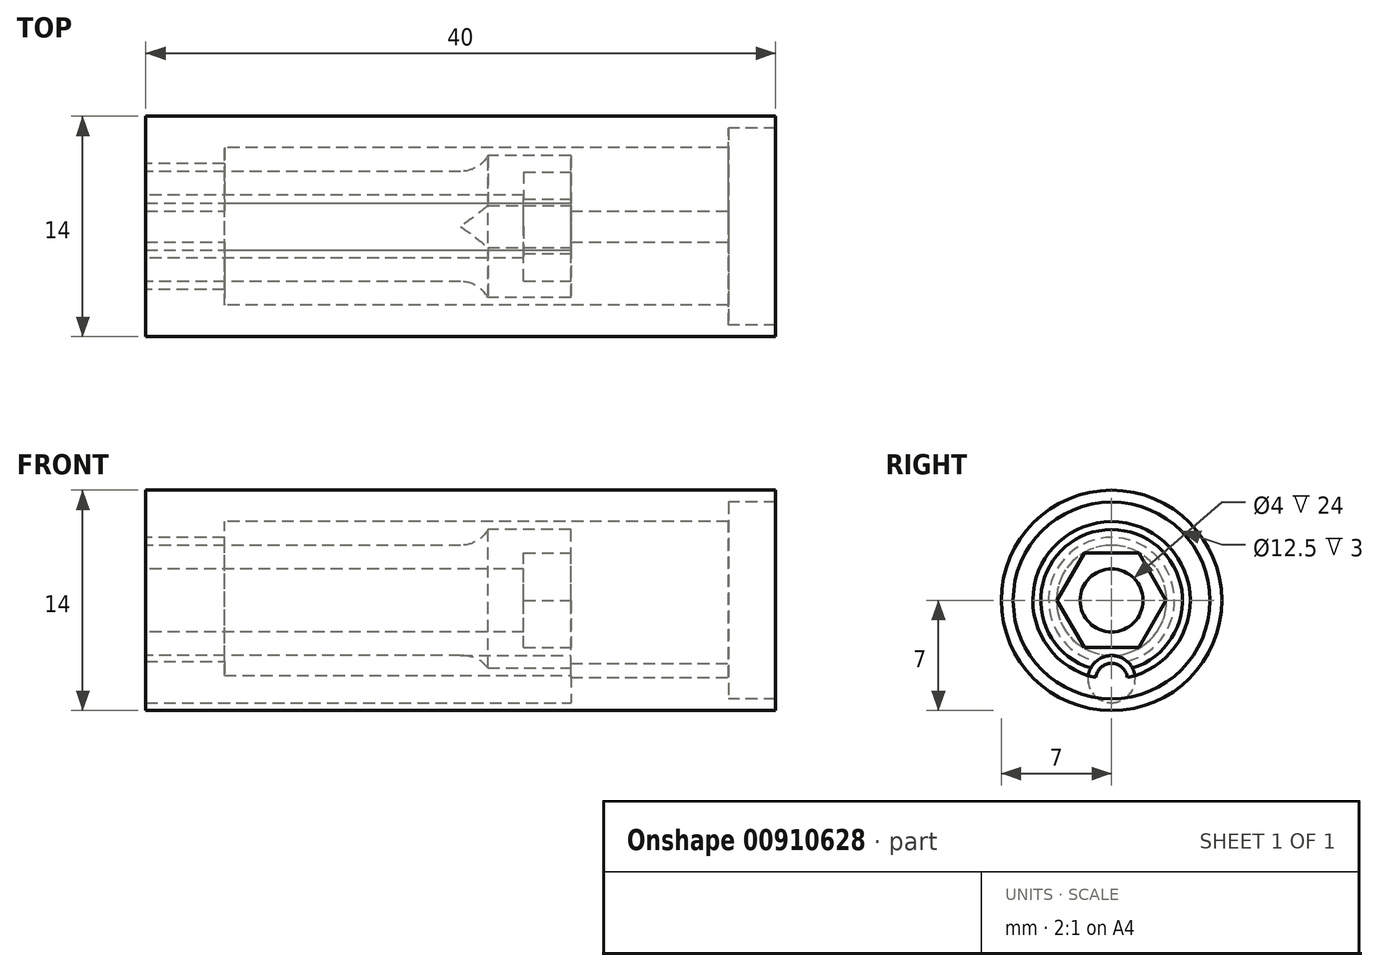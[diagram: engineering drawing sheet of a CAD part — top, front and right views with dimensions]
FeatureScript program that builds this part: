
annotation { "Feature Type Name" : "Feature", "Feature Type Description" : "" }
export const myFeature = defineFeature(function(context is Context, id is Id, definition is map)
    precondition{}
    {
        {
            var Q0;
            Q0=qCreatedBy(makeId("Front.planeOp"),FACE);
            var sketch = newSketch(context, id + "F0", { "sketchPlane" : qUnion([Q0])});
            skLineSegment(sketch, "E0", {"start": v(0, 0) * mm, "end": v(35.36, 0) * mm, "construction": true});
            skLineSegment(sketch, "E1.MirrorCS", {"start": v(40, -7) * mm, "end": v(0, -7) * mm});
            skLineSegment(sketch, "E2.MirrorCS", {"start": v(0, -3.5) * mm, "end": v(0, -2) * mm});
            skLineSegment(sketch, "E3.MirrorCS", {"start": v(0, -2) * mm, "end": v(27, -2) * mm});
            skLineSegment(sketch, "E4", {"start": v(0, -7) * mm, "end": v(0, -4) * mm});
            skLineSegment(sketch, "E5", {"start": v(0, -4) * mm, "end": v(5, -4) * mm});
            skLineSegment(sketch, "E6", {"start": v(5, -4) * mm, "end": v(5, -5) * mm});
            skLineSegment(sketch, "E7", {"start": v(0, -3.5) * mm, "end": v(22, -3.5) * mm});
            skLineSegment(sketch, "E8", {"start": v(22, -3.5) * mm, "end": v(22, -4.5) * mm});
            skLineSegment(sketch, "E9", {"start": v(22, -4.5) * mm, "end": v(27, -4.5) * mm});
            skLineSegment(sketch, "E10", {"start": v(27, -4.5) * mm, "end": v(27, -2) * mm});
            skLineSegment(sketch, "E11", {"start": v(40, -7) * mm, "end": v(40, -6.25) * mm});
            skLineSegment(sketch, "E12", {"start": v(40, -6.25) * mm, "end": v(37, -6.25) * mm});
            skLineSegment(sketch, "E13", {"start": v(37, -6.25) * mm, "end": v(37, -5) * mm});
            skLineSegment(sketch, "E14", {"start": v(37, -5) * mm, "end": v(5, -5) * mm});
            skSolve(sketch);
        }
        {
            var Q0;
            Q0=makeQuery(id+"F0.imprint","IMPRINT",FACE,{"disambiguationData":[TD([[makeQuery(id+"F0.imprint","IMPRINT",EDGE,{"derivedFrom":sQuery(id+"F0.wireOp",EDGE,"E1.MirrorCS")}),-1.0]])]});
            var Q1;
            Q1=makeQuery(id+"F0.imprint","IMPRINT",FACE,{"disambiguationData":[TD([[makeQuery(id+"F0.imprint","IMPRINT",EDGE,{"derivedFrom":sQuery(id+"F0.wireOp",EDGE,"E2.MirrorCS")}),-1.0]])]});
            var Q2;
            Q2=sQuery(id+"F0.wireOp",EDGE,"E0");
            revolve(context, id + "F1", {"surfaceOperationType" : NewSurfaceOperationType.NEW, "entities" : qUnion([Q0, Q1]), "axis" : qUnion([Q2]), "revolveType" : RevolveType.FULL});
        }
        {
            var Q0;
            Q0=makeQuery(id+"F1.opRevolve","SWEPT_FACE",FACE,{"disambiguationData":[OSD([sQuery(id+"F0.wireOp",EDGE,"E13")])]});
            var sketch = newSketch(context, id + "F2", { "sketchPlane" : qUnion([Q0])});
            skCircle(sketch, "E15", {"center": v(0, -5) * mm, "radius": 1 * mm});
            skSolve(sketch);
        }
        {
            var Q0;
            Q0 = qSketchRegion(id + "F2", true);
            var Q1;
            Q1=makeQuery(id+"F1.opRevolve","SWEPT_FACE",FACE,{"disambiguationData":[OSD([sQuery(id+"F0.wireOp",EDGE,"E4")])]});
            extrude(context, id + "F3", {"entities" : qUnion([Q0]), "operationType" : NewBodyOperationType.ADD, "endBound" : BoundingType.UP_TO_SURFACE, "oppositeDirection" : true, "depth" : 25 * mm, "endBoundEntityFace" : qUnion([Q1]), "offsetDistance" : 25 * mm});
        }
        {
            var Q0;
            Q0=makeQuery(id+"F1.opRevolve","SWEPT_EDGE",EDGE,{"disambiguationData":[OSD([sQuery(id+"F0.wireOp",EDGE,"E7"),sQuery(id+"F0.wireOp",EDGE,"E8")])]});
            fillet(context, id + "F4", {"entities" : qUnion([Q0]), "radius" : 2 * mm, "tangentPropagation" : true, "allowEdgeOverflow" : false});
        }
        {
            var Q0;
            Q0=makeQuery(id+"F1.opRevolve","SWEPT_FACE",FACE,{"disambiguationData":[OSD([sQuery(id+"F0.wireOp",EDGE,"E10")])]});
            var sketch = newSketch(context, id + "F5", { "sketchPlane" : qUnion([Q0])});
            skCircle(sketch, "E16", {"center": v(0, -5) * mm, "radius": 1.5 * mm});
            skSolve(sketch);
        }
        {
            var Q0;
            Q0 = qSketchRegion(id + "F5", true);
            extrude(context, id + "F6", {"entities" : qUnion([Q0]), "operationType" : NewBodyOperationType.REMOVE, "endBound" : BoundingType.THROUGH_ALL, "oppositeDirection" : true, "depth" : 25 * mm, "offsetDistance" : 25 * mm});
        }
        {
            var Q0;
            Q0=makeQuery(id+"F1.opRevolve","SWEPT_FACE",FACE,{"disambiguationData":[OSD([sQuery(id+"F0.wireOp",EDGE,"E10")])]});
            var sketch = newSketch(context, id + "F7", { "sketchPlane" : qUnion([Q0])});
            skCircle(sketch, "E17.cCircle", {"center": v(0, 0) * mm, "radius": 3 * mm, "construction": true});
            skLineSegment(sketch, "E17.0", {"start": v(-1.73, 3) * mm, "end": v(1.73, 3) * mm});
            skLineSegment(sketch, "E17.1", {"start": v(1.73, 3) * mm, "end": v(3.46, 0) * mm});
            skLineSegment(sketch, "E17.2", {"start": v(3.46, 0) * mm, "end": v(1.73, -3) * mm});
            skLineSegment(sketch, "E17.3", {"start": v(1.73, -3) * mm, "end": v(-1.73, -3) * mm});
            skLineSegment(sketch, "E17.4", {"start": v(-1.73, -3) * mm, "end": v(-3.46, 0) * mm});
            skLineSegment(sketch, "E17.5", {"start": v(-3.46, 0) * mm, "end": v(-1.73, 3) * mm});
            skPoint(sketch, "E17.0.midPoint", {"position": v(0, 3) * mm});
            skSolve(sketch);
        }
        {
            var Q0;
            Q0 = qSketchRegion(id + "F7", true);
            extrude(context, id + "F8", {"entities" : qUnion([Q0]), "operationType" : NewBodyOperationType.REMOVE, "oppositeDirection" : true, "depth" : 3 * mm, "offsetDistance" : 25 * mm});
        }
    });
